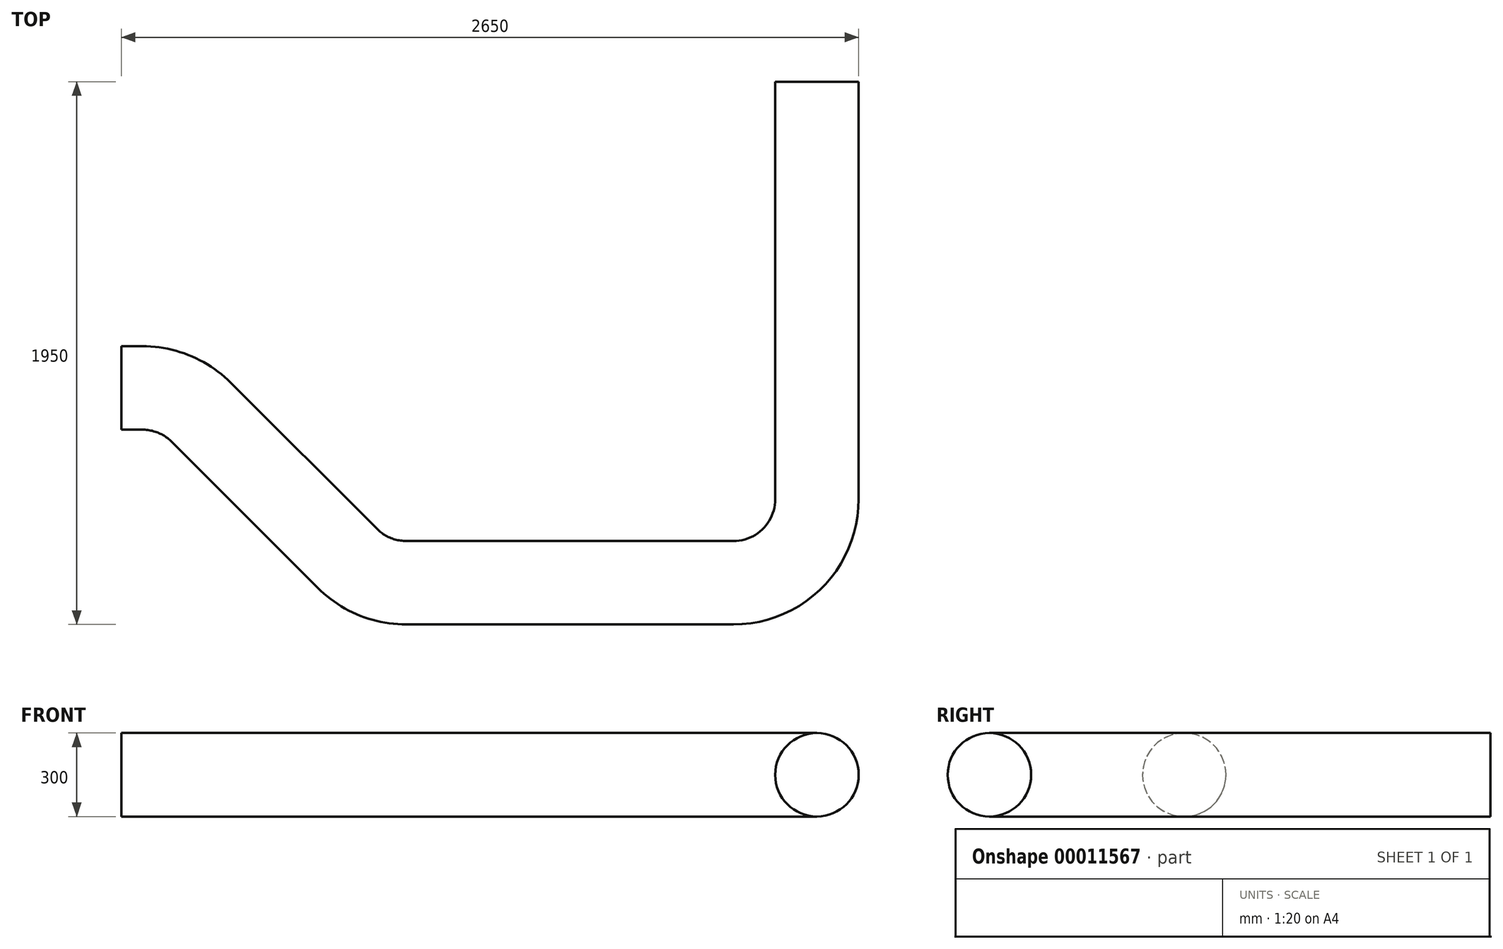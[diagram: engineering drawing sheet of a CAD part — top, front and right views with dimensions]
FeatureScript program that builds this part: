
annotation { "Feature Type Name" : "Feature", "Feature Type Description" : "" }
export const myFeature = defineFeature(function(context is Context, id is Id, definition is map)
    precondition{}
    {
        {
            var Q0;
            Q0=qCreatedBy(makeId("Top.planeOp"),FACE);
            var sketch = newSketch(context, id + "F0", { "sketchPlane" : qUnion([Q0])});
            skLineSegment(sketch, "E0", {"start": v(0, 0) * mm, "end": v(75.74, 0) * mm});
            skLineSegment(sketch, "E1", {"start": v(287.87, -87.87) * mm, "end": v(812.13, -612.13) * mm});
            skLineSegment(sketch, "E2", {"start": v(1024.26, -700) * mm, "end": v(2200, -700) * mm});
            skLineSegment(sketch, "E3", {"start": v(2500, -400) * mm, "end": v(2500, 1100) * mm});
            skPoint(sketch, "E4.visualSharp", {"position": v(200, 0) * mm});
            skArc(sketch, "E4.filletArc", {"start": v(287.87, -87.87) * mm, "mid": v(190.54, -22.84) * mm, "end": v(75.74, 0) * mm});
            skPoint(sketch, "E5.visualSharp", {"position": v(900, -700) * mm});
            skArc(sketch, "E5.filletArc", {"start": v(812.13, -612.13) * mm, "mid": v(909.46, -677.16) * mm, "end": v(1024.26, -700) * mm});
            skPoint(sketch, "E6.visualSharp", {"position": v(2500, -700) * mm});
            skArc(sketch, "E6.filletArc", {"start": v(2200, -700) * mm, "mid": v(2412.13, -612.13) * mm, "end": v(2500, -400) * mm});
            skSolve(sketch);
        }
        {
            var Q0;
            Q0=qCreatedBy(makeId("Right.planeOp"),FACE);
            var sketch = newSketch(context, id + "F1", { "sketchPlane" : qUnion([Q0])});
            skCircle(sketch, "E7", {"center": v(0, 0) * mm, "radius": 150 * mm});
            skSolve(sketch);
        }
        {
            var Q0;
            Q0=qSketchRegion(id+"F1",true);
            var Q1;
            Q1=qBodyType(qCreatedBy(id+"F0",EDGE),BodyType.WIRE);
            sweep(context, id + "F2", {"profiles" : qUnion([Q0]), "path" : qUnion([Q1])});
        }
    });
